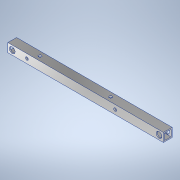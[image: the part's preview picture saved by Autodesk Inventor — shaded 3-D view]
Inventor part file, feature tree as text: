
AUTODESK INVENTOR PART (.ipt)
format: ipt  version: 2020.3 (Build 243373000, 373)  size: 177,152 bytes
history: native  units: mm
features: sketch x7, hole x4, extrude x3, other x1
ambient origin geometry x8: Origin, YZ Plane, XZ Plane, XY Plane, X Axis, Y Axis, Z Axis, Center Point
bodies: Body1 (feature_tree)
feature tree (15):
  other  "ソリッド1"
  extrude  "押し出し1"  Depth=9.0mm
  hole  "穴1"  [1 undecoded]
  hole  "穴2"  [1 undecoded]
  extrude  "押し出し2"  Depth=6.6mm
  extrude  "押し出し3"  Depth=1.2mm
  hole  "穴3"  [1 undecoded]
  hole  "穴4"  [1 undecoded]
  sketch  "スケッチ1"
  sketch  "スケッチ2"
  sketch  "スケッチ3"
  sketch  "スケッチ4"
  sketch  "スケッチ5"
  sketch  "スケッチ6"
  sketch  "スケッチ7"
note: 4 required parameter values undecoded (feature->parameter linkage not recoverable at this tier; creation-order binding heuristic only, values carry confidence <= 0.55)
